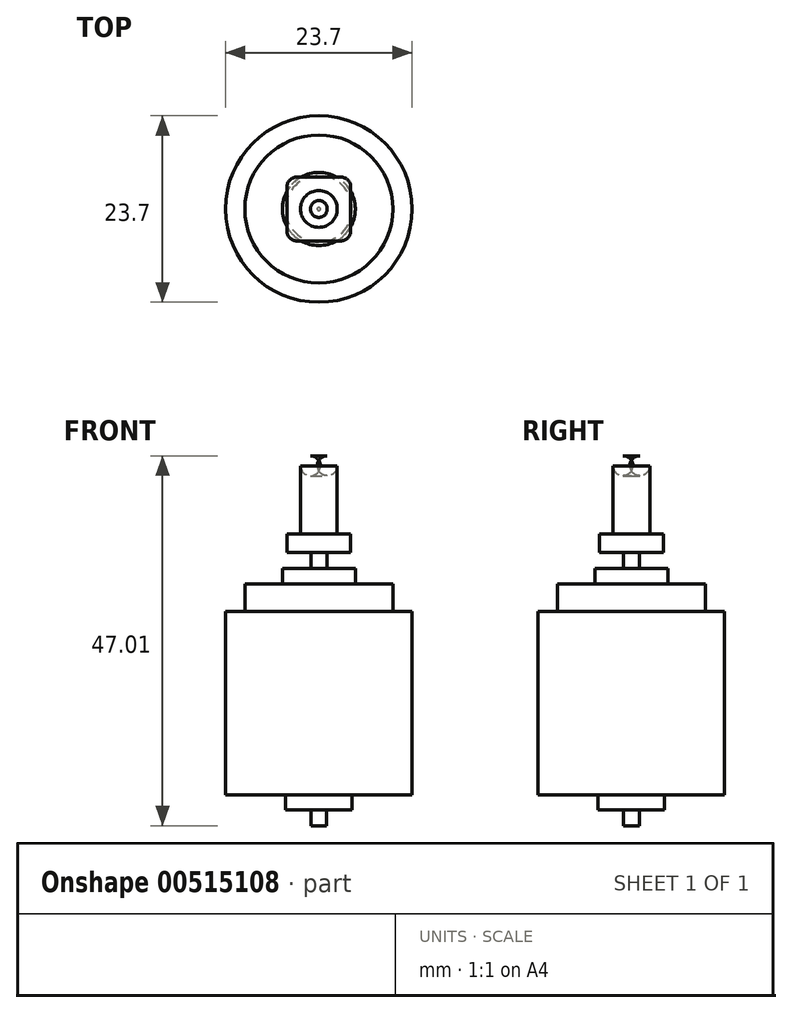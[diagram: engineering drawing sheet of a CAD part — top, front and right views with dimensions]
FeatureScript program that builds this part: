
annotation { "Feature Type Name" : "Feature", "Feature Type Description" : "" }
export const myFeature = defineFeature(function(context is Context, id is Id, definition is map)
    precondition{}
    {
        {
            var Q0;
            Q0=qCreatedBy(makeId("Front.planeOp"),FACE);
            var sketch = newSketch(context, id + "F0", { "sketchPlane" : qUnion([Q0])});
            skLineSegment(sketch, "E0", {"start": v(11.85, 0) * mm, "end": v(11.85, -23.34) * mm});
            skLineSegment(sketch, "E1", {"start": v(11.85, -23.34) * mm, "end": v(4.23, -23.34) * mm});
            skLineSegment(sketch, "E2", {"start": v(4.23, -23.34) * mm, "end": v(4.23, -25.25) * mm});
            skLineSegment(sketch, "E3", {"start": v(4.23, -25.25) * mm, "end": v(1, -25.25) * mm});
            skLineSegment(sketch, "E4", {"start": v(1, -25.25) * mm, "end": v(1, -27.25) * mm});
            skLineSegment(sketch, "E5", {"start": v(1, -27.25) * mm, "end": v(0, -27.25) * mm});
            skLineSegment(sketch, "E6", {"start": v(0, -27.25) * mm, "end": v(0, 19.76) * mm});
            skLineSegment(sketch, "E7", {"start": v(11.85, 0) * mm, "end": v(9.4, 0) * mm});
            skLineSegment(sketch, "E8", {"start": v(9.4, 0) * mm, "end": v(9.4, 3.45) * mm});
            skLineSegment(sketch, "E9", {"start": v(9.4, 3.45) * mm, "end": v(4.64, 3.45) * mm});
            skLineSegment(sketch, "E10", {"start": v(4.64, 3.45) * mm, "end": v(4.64, 5.46) * mm});
            skLineSegment(sketch, "E11", {"start": v(4.64, 5.46) * mm, "end": v(1.02, 5.46) * mm});
            skLineSegment(sketch, "E12", {"start": v(1.02, 5.46) * mm, "end": v(1.02, 7.47) * mm});
            skLineSegment(sketch, "E13", {"start": v(1.02, 7.47) * mm, "end": v(2.34, 7.47) * mm});
            skLineSegment(sketch, "E14", {"start": v(2.34, 7.47) * mm, "end": v(2.34, 19.76) * mm});
            skLineSegment(sketch, "E15", {"start": v(2.34, 19.76) * mm, "end": v(0, 19.76) * mm});
            skLineSegment(sketch, "E16", {"start": v(0, 19.76) * mm, "end": v(0, -27.25) * mm});
            skSolve(sketch);
        }
        {
            var Q0;
            Q0=makeQuery(id+"F0.imprint","IMPRINT",FACE,{"disambiguationData":[TD([[makeQuery(id+"F0.imprint","IMPRINT",EDGE,{"derivedFrom":sQuery(id+"F0.wireOp",EDGE,"E0")}),-1.0]])]});
            var Q1;
            Q1=sQuery(id+"F0.wireOp",EDGE,"E16");
            revolve(context, id + "F1", {"entities" : qUnion([Q0]), "axis" : qUnion([Q1]), "revolveType" : RevolveType.FULL});
        }
        {
            var Q0;
            Q0=makeQuery(id+"F1.opRevolve","SWEPT_FACE",FACE,{"disambiguationData":[OSD([sQuery(id+"F0.wireOp",EDGE,"E13")])]});
            var sketch = newSketch(context, id + "F2", { "sketchPlane" : qUnion([Q0])});
            skLineSegment(sketch, "E17.bottom", {"start": v(4.05, 4.05) * mm, "end": v(-4.05, 4.05) * mm});
            skLineSegment(sketch, "E17.top", {"start": v(4.05, -4.05) * mm, "end": v(-4.05, -4.05) * mm});
            skLineSegment(sketch, "E17.left", {"start": v(4.05, 4.05) * mm, "end": v(4.05, -4.05) * mm});
            skLineSegment(sketch, "E17.right", {"start": v(-4.05, 4.05) * mm, "end": v(-4.05, -4.05) * mm});
            skPoint(sketch, "E17.middle", {"position": v(0, 0) * mm});
            skSolve(sketch);
        }
        {
            var Q0;
            Q0=makeQuery(id+"F2.imprint","IMPRINT",FACE,{"disambiguationData":[TD([[makeQuery(id+"F2.imprint","IMPRINT",EDGE,{"derivedFrom":sQuery(id+"F2.wireOp",EDGE,"E17.bottom")}),1.0]])]});
            extrude(context, id + "F3", {"entities" : qUnion([Q0]), "operationType" : NewBodyOperationType.ADD, "oppositeDirection" : true, "depth" : 2.34 * mm, "offsetDistance" : 25.4 * mm});
        }
        {
            var Q0;
            Q0=makeQuery(id+"F3.opExtrude","SWEPT_EDGE",EDGE,{"disambiguationData":[OSD([sQuery(id+"F2.wireOp",EDGE,"E17.bottom"),sQuery(id+"F2.wireOp",EDGE,"E17.left")])]});
            var Q1;
            Q1=makeQuery(id+"F3.opExtrude","SWEPT_EDGE",EDGE,{"disambiguationData":[OSD([sQuery(id+"F2.wireOp",EDGE,"E17.bottom"),sQuery(id+"F2.wireOp",EDGE,"E17.right")])]});
            var Q2;
            Q2=makeQuery(id+"F3.opExtrude","SWEPT_EDGE",EDGE,{"disambiguationData":[OSD([sQuery(id+"F2.wireOp",EDGE,"E17.top"),sQuery(id+"F2.wireOp",EDGE,"E17.right")])]});
            var Q3;
            Q3=makeQuery(id+"F3.opExtrude","SWEPT_EDGE",EDGE,{"disambiguationData":[OSD([sQuery(id+"F2.wireOp",EDGE,"E17.top"),sQuery(id+"F2.wireOp",EDGE,"E17.left")])]});
            fillet(context, id + "F4", {"entities" : qUnion([Q0, Q1, Q2, Q3]), "radius" : 1.27 * mm, "tangentPropagation" : true, "allowEdgeOverflow" : false});
        }
        {
            var Q0;
            Q0=makeQuery(id+"F1.opRevolve","SWEPT_EDGE",EDGE,{"disambiguationData":[OSD([sQuery(id+"F0.wireOp",EDGE,"E14"),sQuery(id+"F0.wireOp",EDGE,"E15")])]});
            fillet(context, id + "F5", {"entities" : qUnion([Q0]), "radius" : 1.27 * mm, "tangentPropagation" : true, "allowEdgeOverflow" : false});
        }
    });
